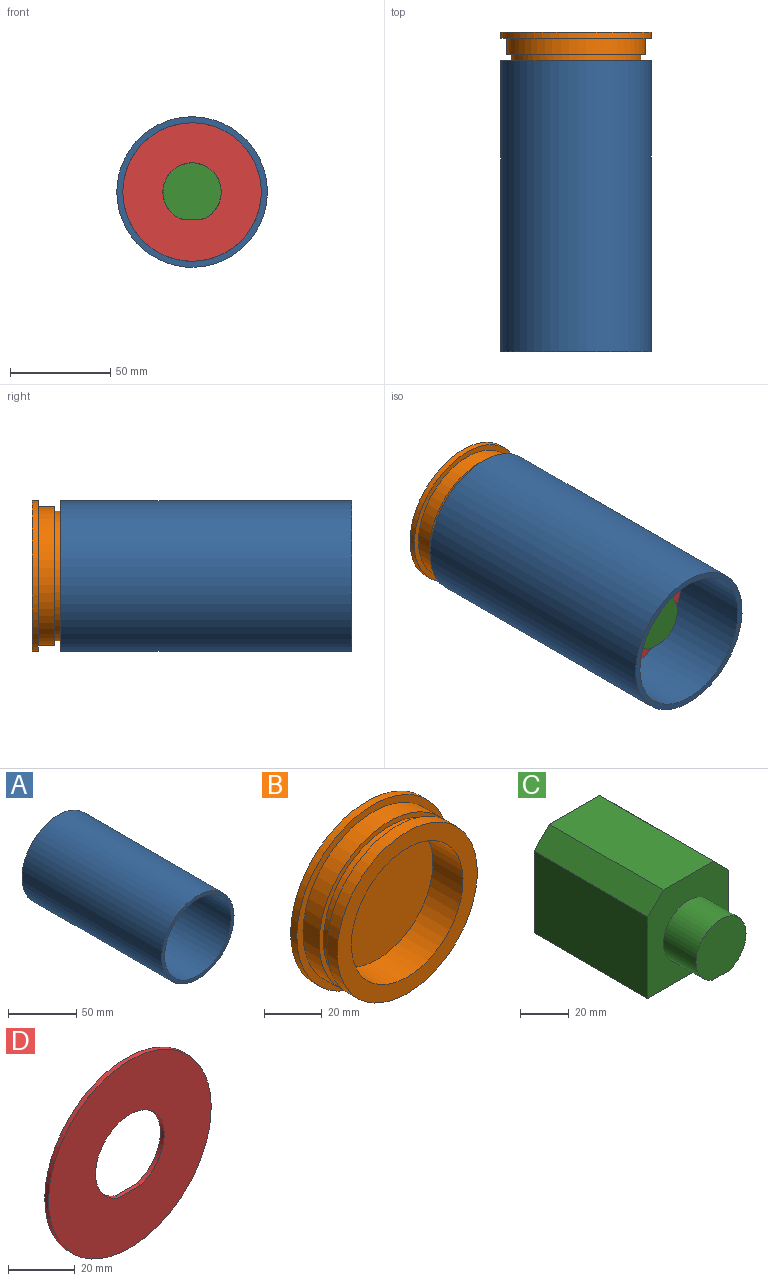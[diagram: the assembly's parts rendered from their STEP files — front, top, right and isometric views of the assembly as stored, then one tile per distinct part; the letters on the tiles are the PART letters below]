
ASSEMBLY  parts=4 mates=5
PART A: 4 faces, bbox 75x145x75 mm
  f0: cylinder r=34.5mm len=145mm, axis (0,-1,0), area 31431.6mm2, adj f2,f3
  f1: cylinder r=37.5mm len=145mm, axis (0,-1,0), area 34164.8mm2, adj f2,f3
  f2: plane 75x75mm, normal (0,1,0), area 678.6mm2, adj f0,f1
  f3: plane 75x75mm, normal (0,-1,0), area 678.6mm2, adj f0,f1
PART B: 11 faces, bbox 74.9x19.8x74.9 mm
  f0: cylinder r=34.45mm len=68.9mm, axis (0,-1,0), area 1082.3mm2, adj f1,f10
  f1: plane 68.9x68.9mm, normal (0,-1,0), area 1361.3mm2, adj f0,f2
  f2: cylinder r=27.45mm len=54.9mm, axis (0,-1,0), area 2552.6mm2, adj f1,f3
  f3: plane 54.9x54.9mm, normal (0,-1,0), area 2367.2mm2, adj f2
  f4: plane 74.88x74.88mm, normal (0,1,0), area 4404.3mm2, adj f5
  f5: cylinder r=37.44mm len=74.88mm, axis (0,-1,0), area 705.8mm2, adj f4,f6
  f6: plane 74.88x74.88mm, normal (0,-1,0), area 675.8mm2, adj f5,f7
  f7: cylinder r=34.45mm len=68.9mm, axis (0,-1,0), area 1731.6mm2, adj f6,f8
  f8: plane 68.9x68.9mm, normal (0,-1,0), area 430.5mm2, adj f7,f9
  f9: cylinder r=32.4mm len=64.8mm, axis (0,-1,0), area 773.6mm2, adj f8,f10
  f10: plane 68.9x68.9mm, normal (0,1,0), area 430.5mm2, adj f0,f9
PART C: 11 faces, bbox 47x84.9x50 mm
  f0: plane 66x47mm, normal (0,0,-1), area 3102mm2, adj f1,f5,f6,f7
  f1: plane 66x41mm, normal (1,0,0), area 2706mm2, adj f0,f2,f6,f7
  f2: plane 66x9mm, normal (0.71,0,0.71), area 840mm2, adj f1,f3,f6,f7
  f3: plane 66x29mm, normal (0,0,1), area 1914mm2, adj f2,f4,f6,f7
  f4: plane 66x9mm, normal (-0.71,0,0.71), area 840mm2, adj f3,f5,f6,f7
  f5: plane 66x41mm, normal (-1,0,0), area 2706mm2, adj f0,f4,f6,f7
  f6: plane 50x47mm, normal (0,1,0), area 2269mm2, adj f0,f1,f2,f3,f4,f5
  f7: plane 50x47mm, normal (0,-1,0), area 1613.9mm2, adj f0,f1,f2,f3,f4,f5,f8,f9
  f8: plane 18.9x9.67mm, normal (0,0,-1), area 182.8mm2, adj f7,f9,f10
  f9: cylinder r=14.5mm len=29mm, axis (0,1,0), area 1535.6mm2, adj f7,f8,f10
  f10: plane 29x28.17mm, normal (0,-1,0), area 655.1mm2, adj f8,f9
PART D: 5 faces, bbox 69x1.6x69 mm
  f0: cylinder r=14.55mm len=29.1mm, axis (0,1,0), area 131mm2, adj f1,f3,f4
  f1: plane 9.4x1.6mm, normal (0,0,1), area 15mm2, adj f0,f3,f4
  f2: cylinder r=34.5mm len=69mm, axis (0,1,0), area 346.8mm2, adj f3,f4
  f3: plane 69x69mm, normal (0,-1,0), area 3079.1mm2, adj f0,f1,f2
  f4: plane 69x69mm, normal (0,1,0), area 3079.1mm2, adj f0,f1,f2
PLACE A rot(axis=(0,-1,0),23.5deg) t=(0,-7.06,13.67)mm fixed
PLACE B rot(axis=(0,-1,0),23.5deg) t=(0,4.05,13.67)mm
PLACE C t=(0,9.45,13.67)mm
PLACE D t=(0,9.45,13.67)mm
MATE parallel D.f1 <-> C.f8  axis (0,0,1) through (0,8.65,-0.1)mm
MATE cylindrical A.f0 <-> B.f0  axis (0,-1,0) through (0,112.94,13.67)mm
MATE cylindrical C.f9 <-> D.f0  axis (0,1,0) through (0,0,13.67)mm
MATE planar C.f7 <-> D.f4  axis (0,-1,0) through (0,9.45,40.62)mm
MATE cylindrical D.f2 <-> A.f0  axis (0,1,0) through (0,8.65,13.67)mm
